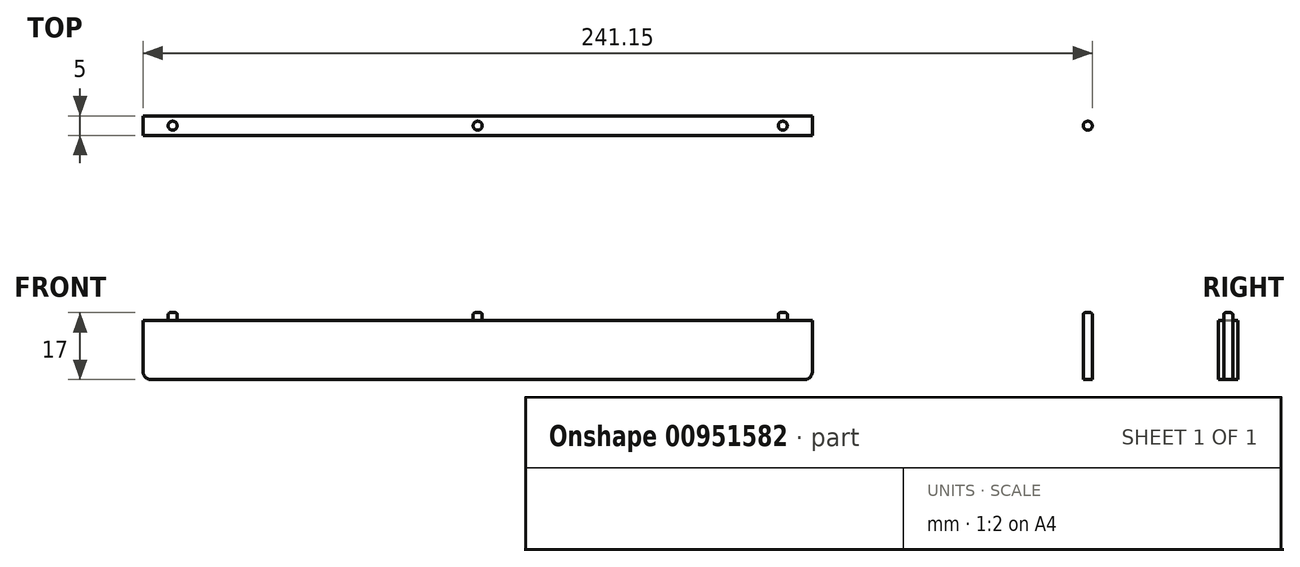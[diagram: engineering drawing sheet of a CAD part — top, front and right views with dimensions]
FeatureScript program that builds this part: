
annotation { "Feature Type Name" : "Feature", "Feature Type Description" : "" }
export const myFeature = defineFeature(function(context is Context, id is Id, definition is map)
    precondition{}
    {
        {
            var Q0;
            Q0=qCreatedBy(makeId("Top.planeOp"),FACE);
            var sketch = newSketch(context, id + "F0", { "sketchPlane" : qUnion([Q0])});
            skLineSegment(sketch, "E0.bottom", {"start": v(85, -2.5) * mm, "end": v(-85, -2.5) * mm});
            skLineSegment(sketch, "E0.top", {"start": v(85, 2.5) * mm, "end": v(-85, 2.5) * mm});
            skLineSegment(sketch, "E0.left", {"start": v(85, -2.5) * mm, "end": v(85, 2.5) * mm});
            skLineSegment(sketch, "E0.right", {"start": v(-85, -2.5) * mm, "end": v(-85, 2.5) * mm});
            skPoint(sketch, "E0.middle", {"position": v(0, 0) * mm});
            skPoint(sketch, "E1", {"position": v(-77.5, 0) * mm});
            skPoint(sketch, "E1.positionSnap0", {"position": v(-85, 0) * mm});
            skPoint(sketch, "E2.2.0.0", {"position": v(77.5, 0) * mm});
            skLineSegment(sketch, "E2.direction1", {"start": v(-77.5, 0) * mm, "end": v(0, 0) * mm, "construction": true});
            skCircle(sketch, "E3", {"center": v(-77.5, 0) * mm, "radius": 1.15 * mm});
            skCircle(sketch, "E4.1.0.0", {"center": v(0, 0) * mm, "radius": 1.15 * mm});
            skCircle(sketch, "E4.2.0.0", {"center": v(77.5, 0) * mm, "radius": 1.15 * mm});
            skCircle(sketch, "E4.3.0.0", {"center": v(155, 0) * mm, "radius": 1.15 * mm});
            skSolve(sketch);
        }
        {
            var Q0;
            Q0=makeQuery(id+"F0.imprint","IMPRINT",FACE,{"disambiguationData":[TD([[makeQuery(id+"F0.imprint","IMPRINT",EDGE,{"derivedFrom":sQuery(id+"F0.wireOp",EDGE,"E0.bottom")}),-1.0]])]});
            extrude(context, id + "F1", {"entities" : qUnion([Q0]), "depth" : 15 * mm, "offsetDistance" : 25 * mm});
        }
        {
            var Q0;
            Q0=makeQuery(id+"F0.imprint","IMPRINT",FACE,{"disambiguationData":[TD([[makeQuery(id+"F0.imprint","IMPRINT",EDGE,{"derivedFrom":sQuery(id+"F0.wireOp",EDGE,"E3")}),1.0]])]});
            var Q1;
            Q1=makeQuery(id+"F0.imprint","IMPRINT",FACE,{"disambiguationData":[TD([[makeQuery(id+"F0.imprint","IMPRINT",EDGE,{"derivedFrom":sQuery(id+"F0.wireOp",EDGE,"E4.1.0.0")}),1.0]])]});
            var Q2;
            Q2=makeQuery(id+"F0.imprint","IMPRINT",FACE,{"disambiguationData":[TD([[makeQuery(id+"F0.imprint","IMPRINT",EDGE,{"derivedFrom":sQuery(id+"F0.wireOp",EDGE,"E4.2.0.0")}),1.0]])]});
            var Q3;
            Q3=makeQuery(id+"F0.imprint","IMPRINT",FACE,{"disambiguationData":[TD([[makeQuery(id+"F0.imprint","IMPRINT",EDGE,{"derivedFrom":sQuery(id+"F0.wireOp",EDGE,"E4.3.0.0")}),1.0]])]});
            extrude(context, id + "F2", {"entities" : qUnion([Q0, Q1, Q2, Q3]), "operationType" : NewBodyOperationType.ADD, "depth" : 17 * mm, "offsetDistance" : 25 * mm});
        }
        {
            var Q0;
            Q0=makeQuery(id+"F2.opExtrude","CAP_EDGE",EDGE,{"disambiguationData":[OSD([sQuery(id+"F0.wireOp",EDGE,"E3")])],"isStart":false});
            var Q1;
            Q1=makeQuery(id+"F2.opExtrude","CAP_EDGE",EDGE,{"disambiguationData":[OSD([sQuery(id+"F0.wireOp",EDGE,"E4.1.0.0")])],"isStart":false});
            var Q2;
            Q2=makeQuery(id+"F2.opExtrude","CAP_EDGE",EDGE,{"disambiguationData":[OSD([sQuery(id+"F0.wireOp",EDGE,"E4.2.0.0")])],"isStart":false});
            var Q3;
            Q3=makeQuery(id+"F2.opExtrude","CAP_EDGE",EDGE,{"disambiguationData":[OSD([sQuery(id+"F0.wireOp",EDGE,"E4.3.0.0")])],"isStart":false});
            fillet(context, id + "F3", {"entities" : qUnion([Q0, Q1, Q2, Q3]), "radius" : 0.5 * mm, "tangentPropagation" : true, "allowEdgeOverflow" : false});
        }
        {
            var Q0;
            Q0=makeQuery(id+"F1.opExtrude","CAP_EDGE",EDGE,{"disambiguationData":[OSD([sQuery(id+"F0.wireOp",EDGE,"E0.right")])],"isStart":true});
            var Q1;
            Q1=makeQuery(id+"F1.opExtrude","CAP_EDGE",EDGE,{"disambiguationData":[OSD([sQuery(id+"F0.wireOp",EDGE,"E0.left")])],"isStart":true});
            fillet(context, id + "F4", {"entities" : qUnion([Q0, Q1]), "radius" : 2 * mm, "tangentPropagation" : true, "allowEdgeOverflow" : false});
        }
    });
